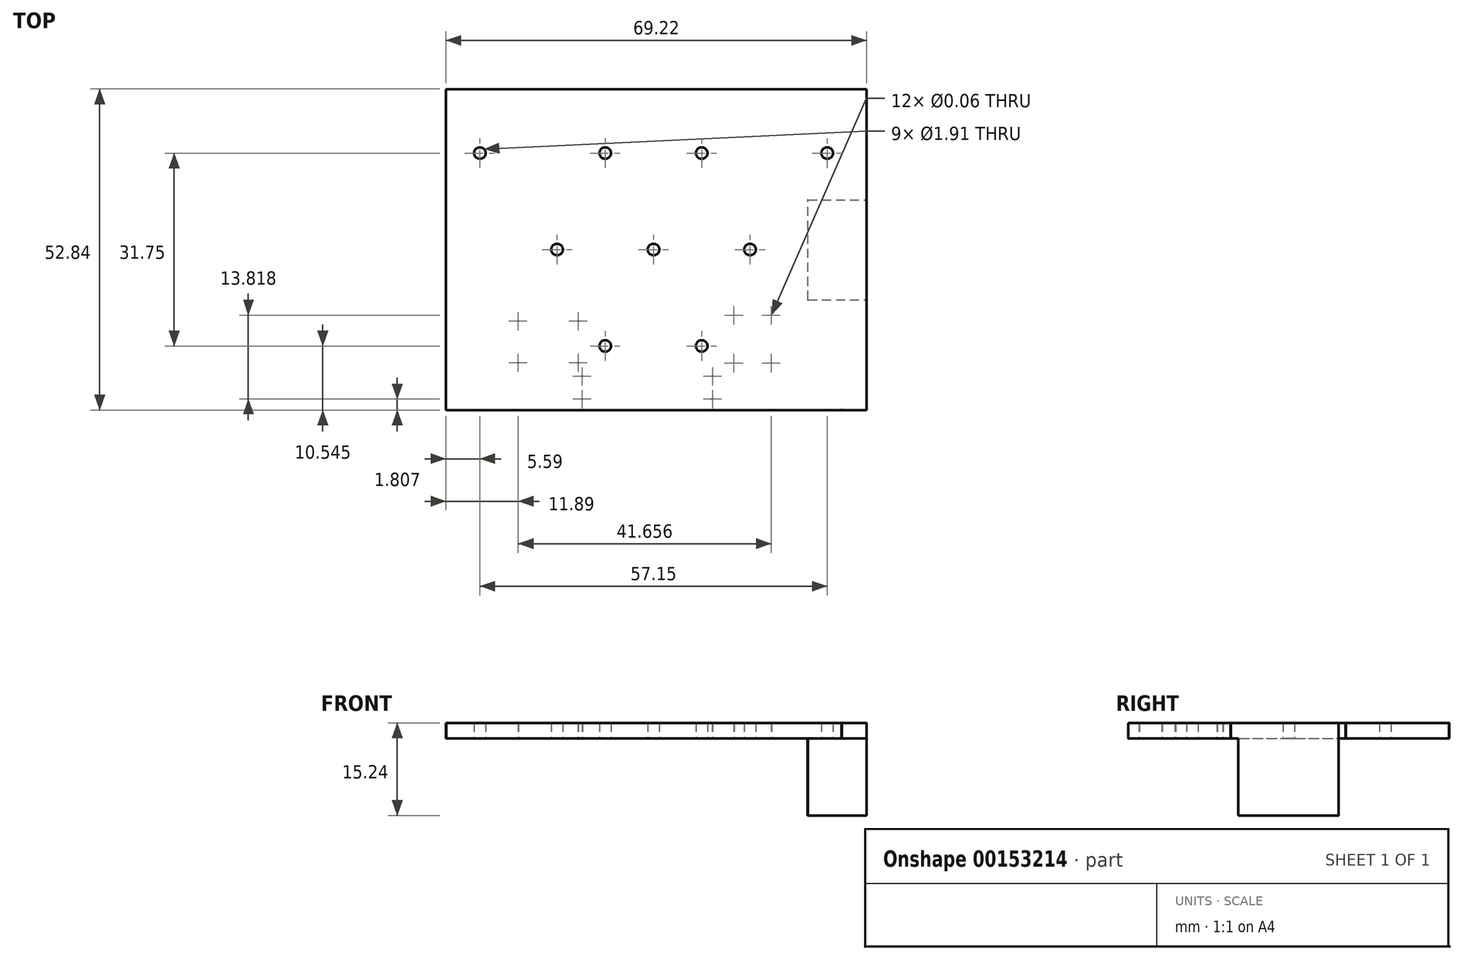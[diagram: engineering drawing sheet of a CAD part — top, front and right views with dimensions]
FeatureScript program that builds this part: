
annotation { "Feature Type Name" : "Feature", "Feature Type Description" : "" }
export const myFeature = defineFeature(function(context is Context, id is Id, definition is map)
    precondition{}
    {
        {
            var Q0;
            Q0=qCreatedBy(makeId("Top.planeOp"),FACE);
            var sketch = newSketch(context, id + "F0", { "sketchPlane" : qUnion([Q0])});
            skLineSegment(sketch, "E0", {"start": v(24.93, -8.3) * mm, "end": v(24.93, 8.18) * mm});
            skArc(sketch, "E1", {"start": v(24.9, -8.3) * mm, "mid": v(24.93, -8.34) * mm, "end": v(24.96, -8.3) * mm});
            skArc(sketch, "E2", {"start": v(24.96, -8.3) * mm, "mid": v(24.93, -8.27) * mm, "end": v(24.9, -8.3) * mm});
            skArc(sketch, "E3", {"start": v(24.9, 8.18) * mm, "mid": v(24.93, 8.15) * mm, "end": v(24.96, 8.18) * mm});
            skArc(sketch, "E4", {"start": v(24.96, 8.18) * mm, "mid": v(24.93, 8.21) * mm, "end": v(24.9, 8.18) * mm});
            skLineSegment(sketch, "E5", {"start": v(24.93, 8.18) * mm, "end": v(34.6, 8.18) * mm});
            skArc(sketch, "E6", {"start": v(34.58, 8.18) * mm, "mid": v(34.6, 8.15) * mm, "end": v(34.64, 8.18) * mm});
            skArc(sketch, "E7", {"start": v(34.64, 8.18) * mm, "mid": v(34.6, 8.21) * mm, "end": v(34.58, 8.18) * mm});
            skLineSegment(sketch, "E8", {"start": v(24.93, -8.3) * mm, "end": v(34.6, -8.3) * mm});
            skArc(sketch, "E9", {"start": v(34.58, -8.3) * mm, "mid": v(34.6, -8.34) * mm, "end": v(34.64, -8.3) * mm});
            skArc(sketch, "E10", {"start": v(34.64, -8.3) * mm, "mid": v(34.6, -8.27) * mm, "end": v(34.58, -8.3) * mm});
            skLineSegment(sketch, "E11", {"start": v(34.6, -9.53) * mm, "end": v(34.6, 9.4) * mm});
            skArc(sketch, "E12", {"start": v(34.58, -9.53) * mm, "mid": v(34.6, -9.56) * mm, "end": v(34.64, -9.53) * mm});
            skArc(sketch, "E13", {"start": v(34.64, -9.53) * mm, "mid": v(34.6, -9.5) * mm, "end": v(34.58, -9.53) * mm});
            skArc(sketch, "E14", {"start": v(34.58, 9.4) * mm, "mid": v(34.6, 9.37) * mm, "end": v(34.64, 9.4) * mm});
            skArc(sketch, "E15", {"start": v(34.64, 9.4) * mm, "mid": v(34.6, 9.43) * mm, "end": v(34.58, 9.4) * mm});
            skLineSegment(sketch, "E16", {"start": v(-12.18, -24.61) * mm, "end": v(-12.18, -20.88) * mm});
            skArc(sketch, "E17", {"start": v(-12.21, -24.61) * mm, "mid": v(-12.18, -24.64) * mm, "end": v(-12.15, -24.61) * mm});
            skArc(sketch, "E18", {"start": v(-12.15, -24.61) * mm, "mid": v(-12.18, -24.58) * mm, "end": v(-12.21, -24.61) * mm});
            skArc(sketch, "E19", {"start": v(-12.21, -20.88) * mm, "mid": v(-12.18, -20.91) * mm, "end": v(-12.15, -20.88) * mm});
            skArc(sketch, "E20", {"start": v(-12.15, -20.88) * mm, "mid": v(-12.18, -20.85) * mm, "end": v(-12.21, -20.88) * mm});
            skLineSegment(sketch, "E21", {"start": v(-12.18, -24.61) * mm, "end": v(9.26, -24.61) * mm});
            skArc(sketch, "E22", {"start": v(9.23, -24.61) * mm, "mid": v(9.26, -24.64) * mm, "end": v(9.3, -24.61) * mm});
            skArc(sketch, "E23", {"start": v(9.3, -24.61) * mm, "mid": v(9.26, -24.58) * mm, "end": v(9.23, -24.61) * mm});
            skLineSegment(sketch, "E24", {"start": v(9.26, -24.61) * mm, "end": v(9.26, -20.88) * mm});
            skArc(sketch, "E25", {"start": v(9.23, -20.88) * mm, "mid": v(9.26, -20.91) * mm, "end": v(9.3, -20.88) * mm});
            skArc(sketch, "E26", {"start": v(9.3, -20.88) * mm, "mid": v(9.26, -20.85) * mm, "end": v(9.23, -20.88) * mm});
            skLineSegment(sketch, "E27", {"start": v(-12.18, -20.88) * mm, "end": v(9.26, -20.88) * mm});
            skLineSegment(sketch, "E28", {"start": v(12.79, -18.67) * mm, "end": v(12.79, -10.8) * mm});
            skArc(sketch, "E29", {"start": v(12.76, -18.67) * mm, "mid": v(12.79, -18.7) * mm, "end": v(12.82, -18.67) * mm});
            skArc(sketch, "E30", {"start": v(12.82, -18.67) * mm, "mid": v(12.79, -18.64) * mm, "end": v(12.76, -18.67) * mm});
            skArc(sketch, "E31", {"start": v(12.76, -10.8) * mm, "mid": v(12.79, -10.83) * mm, "end": v(12.82, -10.8) * mm});
            skArc(sketch, "E32", {"start": v(12.82, -10.8) * mm, "mid": v(12.79, -10.76) * mm, "end": v(12.76, -10.8) * mm});
            skLineSegment(sketch, "E33", {"start": v(12.79, -10.8) * mm, "end": v(18.94, -10.8) * mm});
            skArc(sketch, "E34", {"start": v(18.9, -10.8) * mm, "mid": v(18.94, -10.83) * mm, "end": v(18.97, -10.8) * mm});
            skArc(sketch, "E35", {"start": v(18.97, -10.8) * mm, "mid": v(18.94, -10.76) * mm, "end": v(18.9, -10.8) * mm});
            skLineSegment(sketch, "E36", {"start": v(18.94, -18.67) * mm, "end": v(18.94, -10.8) * mm});
            skArc(sketch, "E37", {"start": v(18.9, -18.67) * mm, "mid": v(18.94, -18.7) * mm, "end": v(18.97, -18.67) * mm});
            skArc(sketch, "E38", {"start": v(18.97, -18.67) * mm, "mid": v(18.94, -18.64) * mm, "end": v(18.9, -18.67) * mm});
            skLineSegment(sketch, "E39", {"start": v(12.79, -18.67) * mm, "end": v(18.94, -18.67) * mm});
            skLineSegment(sketch, "E40", {"start": v(-12.84, -18.64) * mm, "end": v(-12.84, -11.76) * mm});
            skArc(sketch, "E41", {"start": v(-12.87, -18.64) * mm, "mid": v(-12.84, -18.68) * mm, "end": v(-12.8, -18.64) * mm});
            skArc(sketch, "E42", {"start": v(-12.8, -18.64) * mm, "mid": v(-12.84, -18.61) * mm, "end": v(-12.87, -18.64) * mm});
            skArc(sketch, "E43", {"start": v(-12.87, -11.76) * mm, "mid": v(-12.84, -11.8) * mm, "end": v(-12.8, -11.76) * mm});
            skArc(sketch, "E44", {"start": v(-12.8, -11.76) * mm, "mid": v(-12.84, -11.73) * mm, "end": v(-12.87, -11.76) * mm});
            skLineSegment(sketch, "E45", {"start": v(-22.72, -11.76) * mm, "end": v(-12.84, -11.76) * mm});
            skArc(sketch, "E46", {"start": v(-22.75, -11.76) * mm, "mid": v(-22.72, -11.8) * mm, "end": v(-22.69, -11.76) * mm});
            skArc(sketch, "E47", {"start": v(-22.69, -11.76) * mm, "mid": v(-22.72, -11.73) * mm, "end": v(-22.75, -11.76) * mm});
            skLineSegment(sketch, "E48", {"start": v(-22.72, -18.64) * mm, "end": v(-22.72, -11.76) * mm});
            skArc(sketch, "E49", {"start": v(-22.75, -18.64) * mm, "mid": v(-22.72, -18.68) * mm, "end": v(-22.69, -18.64) * mm});
            skArc(sketch, "E50", {"start": v(-22.69, -18.64) * mm, "mid": v(-22.72, -18.61) * mm, "end": v(-22.75, -18.64) * mm});
            skLineSegment(sketch, "E51", {"start": v(-22.72, -18.64) * mm, "end": v(-12.84, -18.64) * mm});
            skLineSegment(sketch, "E52", {"start": v(-34.6, -26.42) * mm, "end": v(30.52, -26.42) * mm});
            skArc(sketch, "E53", {"start": v(-34.64, -26.42) * mm, "mid": v(-34.6, -26.45) * mm, "end": v(-34.58, -26.42) * mm});
            skArc(sketch, "E54", {"start": v(-34.58, -26.42) * mm, "mid": v(-34.6, -26.38) * mm, "end": v(-34.64, -26.42) * mm});
            skArc(sketch, "E55", {"start": v(30.49, -26.42) * mm, "mid": v(30.52, -26.45) * mm, "end": v(30.55, -26.42) * mm});
            skArc(sketch, "E56", {"start": v(30.55, -26.42) * mm, "mid": v(30.52, -26.38) * mm, "end": v(30.49, -26.42) * mm});
            skLineSegment(sketch, "E57", {"start": v(-34.6, -26.42) * mm, "end": v(-34.6, 26.42) * mm});
            skArc(sketch, "E58", {"start": v(-34.64, 26.42) * mm, "mid": v(-34.6, 26.38) * mm, "end": v(-34.58, 26.42) * mm});
            skArc(sketch, "E59", {"start": v(-34.58, 26.42) * mm, "mid": v(-34.6, 26.45) * mm, "end": v(-34.64, 26.42) * mm});
            skLineSegment(sketch, "E60", {"start": v(-34.6, 26.42) * mm, "end": v(34.6, 26.42) * mm});
            skArc(sketch, "E61", {"start": v(34.58, 26.42) * mm, "mid": v(34.6, 26.38) * mm, "end": v(34.64, 26.42) * mm});
            skArc(sketch, "E62", {"start": v(34.64, 26.42) * mm, "mid": v(34.6, 26.45) * mm, "end": v(34.58, 26.42) * mm});
            skLineSegment(sketch, "E63", {"start": v(34.6, 9.4) * mm, "end": v(34.6, 26.42) * mm});
            skLineSegment(sketch, "E64", {"start": v(34.6, -26.42) * mm, "end": v(34.6, -9.52) * mm});
            skArc(sketch, "E65", {"start": v(34.58, -26.42) * mm, "mid": v(34.6, -26.45) * mm, "end": v(34.64, -26.42) * mm});
            skArc(sketch, "E66", {"start": v(34.64, -26.42) * mm, "mid": v(34.6, -26.38) * mm, "end": v(34.58, -26.42) * mm});
            skLineSegment(sketch, "E67", {"start": v(30.52, -26.42) * mm, "end": v(34.6, -26.42) * mm});
            skArc(sketch, "E68", {"start": v(-29.97, 15.88) * mm, "mid": v(-29.02, 14.92) * mm, "end": v(-28.07, 15.88) * mm});
            skArc(sketch, "E69", {"start": v(-28.07, 15.88) * mm, "mid": v(-29.02, 16.83) * mm, "end": v(-29.97, 15.88) * mm});
            skArc(sketch, "E70", {"start": v(-9.35, 15.88) * mm, "mid": v(-8.4, 14.92) * mm, "end": v(-7.44, 15.88) * mm});
            skArc(sketch, "E71", {"start": v(-7.44, 15.88) * mm, "mid": v(-8.4, 16.83) * mm, "end": v(-9.35, 15.88) * mm});
            skArc(sketch, "E72", {"start": v(6.53, 15.88) * mm, "mid": v(7.48, 14.92) * mm, "end": v(8.43, 15.88) * mm});
            skArc(sketch, "E73", {"start": v(8.43, 15.88) * mm, "mid": v(7.48, 16.83) * mm, "end": v(6.53, 15.88) * mm});
            skArc(sketch, "E74", {"start": v(27.18, 15.88) * mm, "mid": v(28.13, 14.92) * mm, "end": v(29.08, 15.88) * mm});
            skArc(sketch, "E75", {"start": v(29.08, 15.88) * mm, "mid": v(28.13, 16.83) * mm, "end": v(27.18, 15.88) * mm});
            skArc(sketch, "E76", {"start": v(14.48, 0) * mm, "mid": v(15.43, -0.95) * mm, "end": v(16.38, 0) * mm});
            skArc(sketch, "E77", {"start": v(16.38, 0) * mm, "mid": v(15.43, 0.95) * mm, "end": v(14.48, 0) * mm});
            skArc(sketch, "E78", {"start": v(-17.27, 0) * mm, "mid": v(-16.32, -0.95) * mm, "end": v(-15.37, 0) * mm});
            skArc(sketch, "E79", {"start": v(-15.37, 0) * mm, "mid": v(-16.32, 0.95) * mm, "end": v(-17.27, 0) * mm});
            skArc(sketch, "E80", {"start": v(-1.4, 0) * mm, "mid": v(-0.44, -0.95) * mm, "end": v(0.5, 0) * mm});
            skArc(sketch, "E81", {"start": v(0.5, 0) * mm, "mid": v(-0.44, 0.95) * mm, "end": v(-1.4, 0) * mm});
            skArc(sketch, "E82", {"start": v(-9.35, -15.88) * mm, "mid": v(-8.4, -16.83) * mm, "end": v(-7.44, -15.88) * mm});
            skArc(sketch, "E83", {"start": v(-7.44, -15.88) * mm, "mid": v(-8.4, -14.92) * mm, "end": v(-9.35, -15.88) * mm});
            skArc(sketch, "E84", {"start": v(6.53, -15.88) * mm, "mid": v(7.48, -16.83) * mm, "end": v(8.43, -15.88) * mm});
            skArc(sketch, "E85", {"start": v(8.43, -15.88) * mm, "mid": v(7.48, -14.92) * mm, "end": v(6.53, -15.88) * mm});
            skSolve(sketch);
        }
        {
            var Q0;
            {var subQ11=sQuery(id+"F0.wireOp",EDGE,"4dfc633e-bc55-4e2a-a4c2-03e747672204");Q0=makeQuery(id+"F0.imprint","IMPRINT",FACE,{"disambiguationData":[TD([[makeQuery(id+"F0.imprint","IMPRINT",EDGE,{"derivedFrom":subQ11}),-1.0]])]});}
            var Q1;
            {var subQ57=sQuery(id+"F0.wireOp",EDGE,"E4");Q1=makeQuery(id+"F0.imprint","IMPRINT",FACE,{"disambiguationData":[TD([[makeQuery(id+"F0.imprint","IMPRINT",EDGE,{"derivedFrom":subQ57}),-1.0]])]});}
            var Q2;
            {var subQ8=sQuery(id+"F0.wireOp",EDGE,"E28");var subQ11=sQuery(id+"F0.wireOp",EDGE,"E30");var subQ12=makeQuery(id+"F0.imprint","INTERSECT",VERTEX,{"derivedFrom":[subQ8,subQ11]});Q2=makeQuery(id+"F0.imprint","IMPRINT",FACE,{"disambiguationData":[TD([[makeQuery(id+"F0.imprint","IMPRINT",EDGE,{"disambiguationData":[TD([[subQ12,-1.0]])],"derivedFrom":subQ8}),-1.0]])]});}
            var Q3;
            {var subQ5=sQuery(id+"F0.wireOp",EDGE,"E18");var subQ9=sQuery(id+"F0.wireOp",EDGE,"E16");var subQ10=makeQuery(id+"F0.imprint","INTERSECT",VERTEX,{"derivedFrom":[subQ9,subQ5]});Q3=makeQuery(id+"F0.imprint","IMPRINT",FACE,{"disambiguationData":[TD([[makeQuery(id+"F0.imprint","IMPRINT",EDGE,{"disambiguationData":[TD([[subQ10,-1.0]])],"derivedFrom":subQ9}),-1.0]])]});}
            var Q4;
            {var subQ9=sQuery(id+"F0.wireOp",EDGE,"E40");var subQ11=sQuery(id+"F0.wireOp",EDGE,"E42");var subQ12=makeQuery(id+"F0.imprint","INTERSECT",VERTEX,{"derivedFrom":[subQ9,subQ11]});Q4=makeQuery(id+"F0.imprint","IMPRINT",FACE,{"disambiguationData":[TD([[makeQuery(id+"F0.imprint","IMPRINT",EDGE,{"disambiguationData":[TD([[subQ12,-1.0]])],"derivedFrom":subQ9}),1.0]])]});}
            extrude(context, id + "F1", {"entities" : qUnion([Q0, Q1, Q2, Q3, Q4]), "depth" : 2.54 * mm});
        }
        {
            var Q0;
            Q0=makeQuery(id+"F1.opExtrude","CAP_FACE",FACE,{"disambiguationData":[OSD([sQuery(id+"F0.wireOp",EDGE,"E0"),sQuery(id+"F0.wireOp",EDGE,"E5"),sQuery(id+"F0.wireOp",EDGE,"E3"),sQuery(id+"F0.wireOp",EDGE,"E4"),sQuery(id+"F0.wireOp",EDGE,"E7"),sQuery(id+"F0.wireOp",EDGE,"E8"),sQuery(id+"F0.wireOp",EDGE,"E1"),sQuery(id+"F0.wireOp",EDGE,"E2"),sQuery(id+"F0.wireOp",EDGE,"E9"),sQuery(id+"F0.wireOp",EDGE,"E11"),sQuery(id+"F0.wireOp",EDGE,"E17"),sQuery(id+"F0.wireOp",EDGE,"E18"),sQuery(id+"F0.wireOp",EDGE,"E22"),sQuery(id+"F0.wireOp",EDGE,"E23"),sQuery(id+"F0.wireOp",EDGE,"E19"),sQuery(id+"F0.wireOp",EDGE,"E20"),sQuery(id+"F0.wireOp",EDGE,"E25"),sQuery(id+"F0.wireOp",EDGE,"E26"),sQuery(id+"F0.wireOp",EDGE,"E31"),sQuery(id+"F0.wireOp",EDGE,"E32"),sQuery(id+"F0.wireOp",EDGE,"E34"),sQuery(id+"F0.wireOp",EDGE,"E35"),sQuery(id+"F0.wireOp",EDGE,"E29"),sQuery(id+"F0.wireOp",EDGE,"E30"),sQuery(id+"F0.wireOp",EDGE,"E37"),sQuery(id+"F0.wireOp",EDGE,"E38"),sQuery(id+"F0.wireOp",EDGE,"E43"),sQuery(id+"F0.wireOp",EDGE,"E44"),sQuery(id+"F0.wireOp",EDGE,"E46"),sQuery(id+"F0.wireOp",EDGE,"E47"),sQuery(id+"F0.wireOp",EDGE,"E49"),sQuery(id+"F0.wireOp",EDGE,"E50"),sQuery(id+"F0.wireOp",EDGE,"E41"),sQuery(id+"F0.wireOp",EDGE,"E42"),sQuery(id+"F0.wireOp",EDGE,"E52"),sQuery(id+"F0.wireOp",EDGE,"E57"),sQuery(id+"F0.wireOp",EDGE,"E54"),sQuery(id+"F0.wireOp",EDGE,"E60"),sQuery(id+"F0.wireOp",EDGE,"E58"),sQuery(id+"F0.wireOp",EDGE,"E63"),sQuery(id+"F0.wireOp",EDGE,"E14"),sQuery(id+"F0.wireOp",EDGE,"E15"),sQuery(id+"F0.wireOp",EDGE,"E61"),sQuery(id+"F0.wireOp",EDGE,"E64"),sQuery(id+"F0.wireOp",EDGE,"E12"),sQuery(id+"F0.wireOp",EDGE,"E13"),sQuery(id+"F0.wireOp",EDGE,"E67"),sQuery(id+"F0.wireOp",EDGE,"E56"),sQuery(id+"F0.wireOp",EDGE,"E66"),sQuery(id+"F0.wireOp",EDGE,"E68"),sQuery(id+"F0.wireOp",EDGE,"E69"),sQuery(id+"F0.wireOp",EDGE,"E70"),sQuery(id+"F0.wireOp",EDGE,"E71"),sQuery(id+"F0.wireOp",EDGE,"E72"),sQuery(id+"F0.wireOp",EDGE,"E73"),sQuery(id+"F0.wireOp",EDGE,"E74"),sQuery(id+"F0.wireOp",EDGE,"E75"),sQuery(id+"F0.wireOp",EDGE,"E76"),sQuery(id+"F0.wireOp",EDGE,"E77"),sQuery(id+"F0.wireOp",EDGE,"E78"),sQuery(id+"F0.wireOp",EDGE,"E79"),sQuery(id+"F0.wireOp",EDGE,"E80"),sQuery(id+"F0.wireOp",EDGE,"E81"),sQuery(id+"F0.wireOp",EDGE,"E82"),sQuery(id+"F0.wireOp",EDGE,"E83"),sQuery(id+"F0.wireOp",EDGE,"E84"),sQuery(id+"F0.wireOp",EDGE,"E85")])],"isStart":true});
            var sketch = newSketch(context, id + "F2", { "sketchPlane" : qUnion([Q0])});
            skLineSegment(sketch, "E86", {"start": v(34.58, -8.18) * mm, "end": v(34.6, 8.34) * mm});
            skSolve(sketch);
        }
        {
            var Q0;
            Q0=makeQuery(id+"F2.imprint","IMPRINT",FACE,{"disambiguationData":[TD([[makeQuery(id+"F2.imprint","IMPRINT",EDGE,{"derivedFrom":sQuery(id+"F2.wireOp",EDGE,"E86")}),1.0]])]});
            extrude(context, id + "F3", {"entities" : qUnion([Q0]), "operationType" : NewBodyOperationType.ADD, "depth" : 12.7 * mm});
        }
        {
            var Q0;
            Q0=makeQuery(id+"F3.opExtrude","CAP_FACE",FACE,{"disambiguationData":[OSD([sQuery(id+"F0.wireOp",EDGE,"E0"),sQuery(id+"F0.wireOp",EDGE,"E5"),sQuery(id+"F0.wireOp",EDGE,"E3"),sQuery(id+"F0.wireOp",EDGE,"E4"),sQuery(id+"F0.wireOp",EDGE,"E8"),sQuery(id+"F0.wireOp",EDGE,"E1"),sQuery(id+"F0.wireOp",EDGE,"E2"),sQuery(id+"F0.wireOp",EDGE,"E9"),sQuery(id+"F2.wireOp",EDGE,"E86")])],"isStart":true});
            extrude(context, id + "F4", {"entities" : qUnion([Q0]), "operationType" : NewBodyOperationType.ADD, "depth" : 2.54 * mm});
        }
    });
